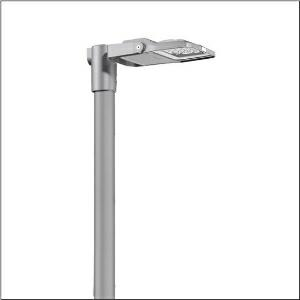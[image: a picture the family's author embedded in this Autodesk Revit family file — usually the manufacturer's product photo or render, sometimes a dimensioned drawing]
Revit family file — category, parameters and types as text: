
# Revit family: floodlight_fl_21_micro___pl52_5xa7762a4d3a_889a
name_source: partatom
category: Lighting Fixtures
units: mm (PartAtom-declared; Revit-internal decimal feet)

## family parameters
Cut with Voids When Loaded = No
Host = Face
Light Source = No
Part Type = Normal
Room Calculation Point = No
Round Connector Dimension = Use Diameter
Shared = No

## types (1)
- --- (1 x LED, 3010 lm, 23.1 W, 4000K)
    Apparent Load = 23 VA
    CIE Flux Codes = 26 60 98 100 100
    Color Rendering = 70
    Color Temperature = 4000K
    Default Elevation = 1800 mm
    Description = Floodlight FL 21 micro, floodlight, primary light control with lens, of PMMA, primary optical cover: protective disc, of toughened safety glass, transparent, light distribution: PL52, light emission: direct distribution, installation type: surface-mounted, LED, High Power LED, rated luminous flux: 3.010lm, luminous efficacy: 130lm/W, light colour: 740, colour temperature: 4000K, control gear: ECG iQ, control: Auto-Match, Temp-Guard, Night-Set, Smart-Wire, Desk-Remote (wireless, voltage-free reading and setting of iQ features in the workshop via application-optimized NFC function/RFID function), optimised constant luminous flux control (CLO 2.0), Street-Remote, with terminal, 6-pole, mains connection: 220..240V, AC, 50/60Hz, start of lifetime: 23W, end of lifetime: 24W, reduction: 11W, luminaire housing, of diecast aluminium, powder-coated, Siteco® metallic grey (DB 702S), corrosivity category C5 according to DIN EN ISO 12944, mast bracket, of steel, galvanised, powder-coated, Siteco® metallic grey (DB 702S), protection rating (complete): IP66, insulation class (complete): insulation class II (safety insulation), certification: CE, protection symbol: D, impact resistance: IK07, permissible operating ambient temperature: -40..+40°C, permissible operating ambient temperature for outdoor applications: -40..+50°C, standard: DIN EN 12944, packaging unit: 1 piece

Light Distribution: PL52
    Height = 65 mm
    Lamp = 1 x LED
    Lamp Light Flux = 3010 lm
    Lamp Power = 23.1 W
    Lamp count = 1
    Length = 312 mm
    Luminous efficacy = 130 lm/W
    Manufacturer = Siteco
    ModVariant = No
    Model = 5XA7762A4D3A
    Number of Poles = 1
    OnlyDefault = Yes
    Power Factor = 1
    Product Name = Floodlight FL 21 micro | PL52
    Product group = floodlight | pylon top
    ProductGroupID = 6101
    Protection Class = Protection class II
    Protection Degree = IP 66
    RLX_Detail_Level = 1
    RlxData = <blob elided: 101861 chars, md5=2c4d9ab6>
    Socket = socket
    Standby Power = 0 W
    System Light Flux = 3010 lm
    System Power = 23 W
    Type Comments = factory setting: luminous flux: 100 % | dim-lin: 254 | 455 mA
    Type Image = l_1007121.jpg
    URL = http://relux.com
    VarID = @adj_090433
    Voltage = 0 V
    Weight = 0.00 kg
    Width = 230 mm

## geometry (parser evidence)
native form markers: Blend x4, Sweep x10
no freeform markers — native parametric forms only
